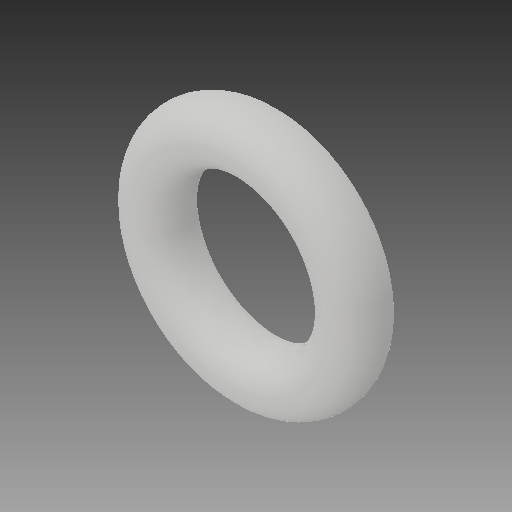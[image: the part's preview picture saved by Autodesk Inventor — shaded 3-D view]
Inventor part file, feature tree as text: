
AUTODESK INVENTOR PART (.ipt)
format: ipt  version: 2019.4 (Build 234330000, 330)  size: 155,136 bytes
history: native  units: in
note: dims shown in document units (in); Inventor stores cm internally (conversion verified against a paired STEP export)
features: revolve x1
ambient origin geometry x8: Origin, YZ Plane, XZ Plane, XY Plane, X Axis, Y Axis, Z Axis, Center Point
bodies: Solid1 (feature_tree)
feature tree (1):
  revolve  "Revolve1"  [1 undecoded]
note: 1 required parameter value undecoded (feature->parameter linkage not recoverable at this tier; creation-order binding heuristic only, values carry confidence <= 0.55)
